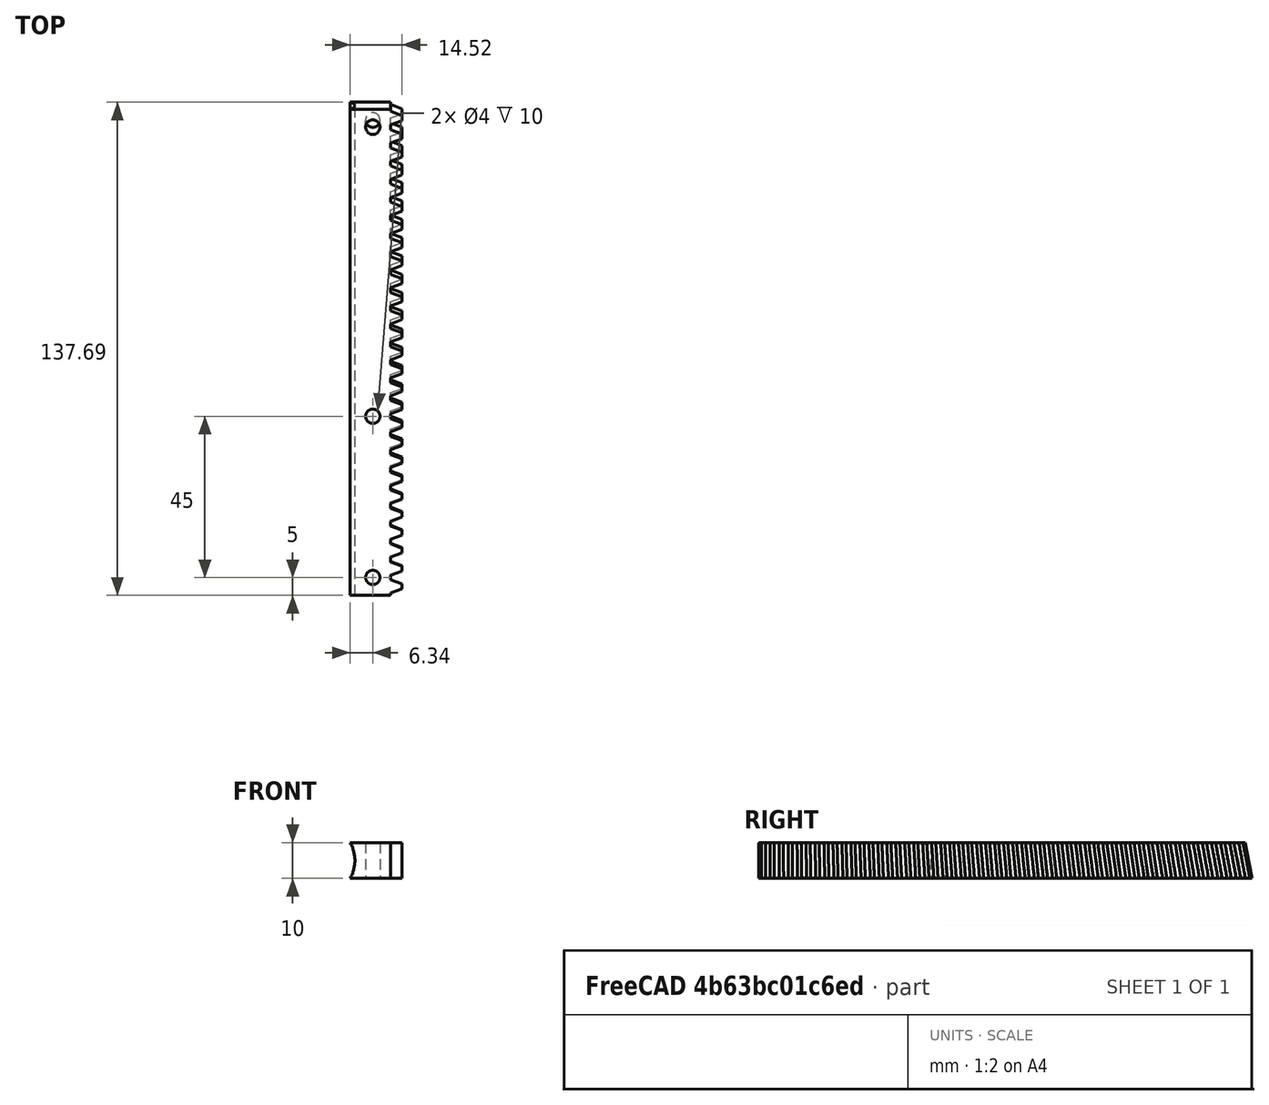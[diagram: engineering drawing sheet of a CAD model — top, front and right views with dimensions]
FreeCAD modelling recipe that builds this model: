
FCSTD DOCUMENT  (FreeCAD 0.17R13522 (Git))
Label: turnrack-rev
License: All rights reserved
LicenseURL: http://en.wikipedia.org/wiki/All_rights_reserved
objects: Part::FeaturePython×27, Part::Cylinder×5, Part::MultiFuse×3, Part::Box×2, Part::Cut×1, Part::Mirroring×1
note: 39 computed .brp shape members not serialized (recipe doc carries the construction recipe); baked Part::Feature solids carry a one-line shape summary decoded from their .brp

FEATURE [Part::FeaturePython] InvoluteRack007  # WARN: FeaturePython — macro-defined, semantics opaque (R4)
  Placement = pos=(0,35.012,0) rot=(0,0,1;0rad)
  beta = 2.91667
  double_helix = false
  head = 0
  height = 10
  module = 1.59155
  pressure_angle = 20
  teeth = 1
  thickness = 10
FEATURE [Part::FeaturePython] InvoluteRack  # WARN: FeaturePython — macro-defined, semantics opaque (R4)
  beta = 0
  double_helix = false
  head = 0
  height = 10
  module = 1.59155
  pressure_angle = 20
  teeth = 1
  thickness = 10
FEATURE [Part::FeaturePython] InvoluteRack004  # WARN: FeaturePython — macro-defined, semantics opaque (R4)
  Placement = pos=(0,20.0019,0) rot=(0,0,1;0rad)
  beta = 1.66667
  double_helix = false
  head = 0
  height = 10
  module = 1.59155
  pressure_angle = 20
  teeth = 1
  thickness = 10
FEATURE [Part::FeaturePython] InvoluteRack003  # WARN: FeaturePython — macro-defined, semantics opaque (R4)
  Placement = pos=(0,15.0007,0) rot=(0,0,1;0rad)
  beta = 1.25
  double_helix = false
  head = 0
  height = 10
  module = 1.59155
  pressure_angle = 20
  teeth = 1
  thickness = 10
FEATURE [Part::FeaturePython] InvoluteRack002  # WARN: FeaturePython — macro-defined, semantics opaque (R4)
  Placement = pos=(0,10.0001,0) rot=(0,0,1;0rad)
  beta = 0.833333
  double_helix = false
  head = 0
  height = 10
  module = 1.59155
  pressure_angle = 20
  teeth = 1
  thickness = 10
FEATURE [Part::FeaturePython] InvoluteRack005  # WARN: FeaturePython — macro-defined, semantics opaque (R4)
  Placement = pos=(0,25.004,0) rot=(0,0,1;0rad)
  beta = 2.08333
  double_helix = false
  head = 0
  height = 10
  module = 1.59155
  pressure_angle = 20
  teeth = 1
  thickness = 10
FEATURE [Part::FeaturePython] InvoluteRack006  # WARN: FeaturePython — macro-defined, semantics opaque (R4)
  Placement = pos=(0,30.0073,0) rot=(0,0,1;0rad)
  beta = 2.5
  double_helix = false
  head = 0
  height = 10
  module = 1.59155
  pressure_angle = 20
  teeth = 1
  thickness = 10
FEATURE [Part::FeaturePython] InvoluteRack001  # WARN: FeaturePython — macro-defined, semantics opaque (R4)
  Placement = pos=(0,5,0) rot=(0,0,1;0rad)
  beta = 0.416667
  double_helix = false
  head = 0
  height = 10
  module = 1.59155
  pressure_angle = 20
  teeth = 1
  thickness = 10
FEATURE [Part::FeaturePython] InvoluteRack008  # WARN: FeaturePython — macro-defined, semantics opaque (R4)
  Placement = pos=(0,40.0185,0) rot=(0,0,1;0rad)
  beta = 3.33333
  double_helix = false
  head = 0
  height = 10
  module = 1.59155
  pressure_angle = 20
  teeth = 1
  thickness = 10
FEATURE [Part::FeaturePython] InvoluteRack009  # WARN: FeaturePython — macro-defined, semantics opaque (R4)
  Placement = pos=(0,45.027,0) rot=(0,0,1;0rad)
  beta = 3.75
  double_helix = false
  head = 0
  height = 10
  module = 1.59155
  pressure_angle = 20
  teeth = 1
  thickness = 10
FEATURE [Part::FeaturePython] InvoluteRack010  # WARN: FeaturePython — macro-defined, semantics opaque (R4)
  Placement = pos=(0,50.0377,0) rot=(0,0,1;0rad)
  beta = 4.16667
  double_helix = false
  head = 0
  height = 10
  module = 1.59155
  pressure_angle = 20
  teeth = 1
  thickness = 10
FEATURE [Part::FeaturePython] InvoluteRack011  # WARN: FeaturePython — macro-defined, semantics opaque (R4)
  Placement = pos=(0,55.051,0) rot=(0,0,1;0rad)
  beta = 4.58333
  double_helix = false
  head = 0
  height = 10
  module = 1.59155
  pressure_angle = 20
  teeth = 1
  thickness = 10
FEATURE [Part::FeaturePython] InvoluteRack012  # WARN: FeaturePython — macro-defined, semantics opaque (R4)
  Placement = pos=(0,60.067,0) rot=(0,0,1;0rad)
  beta = 5
  double_helix = false
  head = 0
  height = 10
  module = 1.59155
  pressure_angle = 20
  teeth = 1
  thickness = 10
FEATURE [Part::FeaturePython] InvoluteRack013  # WARN: FeaturePython — macro-defined, semantics opaque (R4)
  Placement = pos=(0,65.0861,0) rot=(0,0,1;0rad)
  beta = 5.41667
  double_helix = false
  head = 0
  height = 10
  module = 1.59155
  pressure_angle = 20
  teeth = 1
  thickness = 10
FEATURE [Part::FeaturePython] InvoluteRack014  # WARN: FeaturePython — macro-defined, semantics opaque (R4)
  Placement = pos=(0,70.1085,0) rot=(0,0,1;0rad)
  beta = 5.83333
  double_helix = false
  head = 0
  height = 10
  module = 1.59155
  pressure_angle = 20
  teeth = 1
  thickness = 10
FEATURE [Part::FeaturePython] InvoluteRack015  # WARN: FeaturePython — macro-defined, semantics opaque (R4)
  Placement = pos=(0,75.1346,0) rot=(0,0,1;0rad)
  beta = 6.25
  double_helix = false
  head = 0
  height = 10
  module = 1.59155
  pressure_angle = 20
  teeth = 1
  thickness = 10
FEATURE [Part::FeaturePython] InvoluteRack016  # WARN: FeaturePython — macro-defined, semantics opaque (R4)
  Placement = pos=(0,80.1645,0) rot=(0,0,1;0rad)
  beta = 6.66667
  double_helix = false
  head = 0
  height = 10
  module = 1.59155
  pressure_angle = 20
  teeth = 1
  thickness = 10
FEATURE [Part::FeaturePython] InvoluteRack017  # WARN: FeaturePython — macro-defined, semantics opaque (R4)
  Placement = pos=(0,85.1985,0) rot=(0,0,1;0rad)
  beta = 7.08333
  double_helix = false
  head = 0
  height = 10
  module = 1.59155
  pressure_angle = 20
  teeth = 1
  thickness = 10
FEATURE [Part::FeaturePython] InvoluteRack018  # WARN: FeaturePython — macro-defined, semantics opaque (R4)
  Placement = pos=(0,90.237,0) rot=(0,0,1;0rad)
  beta = 7.5
  double_helix = false
  head = 0
  height = 10
  module = 1.59155
  pressure_angle = 20
  teeth = 1
  thickness = 10
FEATURE [Part::FeaturePython] InvoluteRack019  # WARN: FeaturePython — macro-defined, semantics opaque (R4)
  Placement = pos=(0,95.2801,0) rot=(0,0,1;0rad)
  beta = 7.91667
  double_helix = false
  head = 0
  height = 10
  module = 1.59155
  pressure_angle = 20
  teeth = 1
  thickness = 10
FEATURE [Part::FeaturePython] InvoluteRack020  # WARN: FeaturePython — macro-defined, semantics opaque (R4)
  Placement = pos=(0,100.328,0) rot=(0,0,1;0rad)
  beta = 8.33333
  double_helix = false
  head = 0
  height = 10
  module = 1.59155
  pressure_angle = 20
  teeth = 1
  thickness = 10
FEATURE [Part::FeaturePython] InvoluteRack021  # WARN: FeaturePython — macro-defined, semantics opaque (R4)
  Placement = pos=(0,105.382,0) rot=(0,0,1;0rad)
  beta = 8.75
  double_helix = false
  head = 0
  height = 10
  module = 1.59155
  pressure_angle = 20
  teeth = 1
  thickness = 10
FEATURE [Part::FeaturePython] InvoluteRack022  # WARN: FeaturePython — macro-defined, semantics opaque (R4)
  Placement = pos=(0,110.44,0) rot=(0,0,1;0rad)
  beta = 9.16667
  double_helix = false
  head = 0
  height = 10
  module = 1.59155
  pressure_angle = 20
  teeth = 1
  thickness = 10
FEATURE [Part::FeaturePython] InvoluteRack023  # WARN: FeaturePython — macro-defined, semantics opaque (R4)
  Placement = pos=(0,115.505,0) rot=(0,0,1;0rad)
  beta = 9.58333
  double_helix = false
  head = 0
  height = 10
  module = 1.59155
  pressure_angle = 20
  teeth = 1
  thickness = 10
FEATURE [Part::FeaturePython] InvoluteRack024  # WARN: FeaturePython — macro-defined, semantics opaque (R4)
  Placement = pos=(0,120.576,0) rot=(0,0,1;0rad)
  beta = 10
  double_helix = false
  head = 0
  height = 10
  module = 1.59155
  pressure_angle = 20
  teeth = 1
  thickness = 10
FEATURE [Part::FeaturePython] InvoluteRack025  # WARN: FeaturePython — macro-defined, semantics opaque (R4)
  Placement = pos=(0,125.653,0) rot=(0,0,1;0rad)
  beta = 10.4167
  double_helix = false
  head = 0
  height = 10
  module = 1.59155
  pressure_angle = 20
  teeth = 1
  thickness = 10
FEATURE [Part::FeaturePython] InvoluteRack026  # WARN: FeaturePython — macro-defined, semantics opaque (R4)
  Placement = pos=(0,130.737,0) rot=(0,0,1;0rad)
  beta = 10.8333
  double_helix = false
  head = 0
  height = 10
  module = 1.59155
  pressure_angle = 20
  teeth = 1
  thickness = 10
FEATURE [Part::MultiFuse] Union  label="Linear Beta Rack"
  Placement = pos=(11.5915,2.5,0) rot=(0,0,1;0rad)
  Shapes = -> [InvoluteRack,InvoluteRack001,InvoluteRack002,InvoluteRack003,InvoluteRack004,InvoluteRack005,InvoluteRack006,InvoluteRack007,InvoluteRack008,InvoluteRack009,InvoluteRack010,InvoluteRack011,InvoluteRack012,InvoluteRack013,InvoluteRack014,InvoluteRack015,InvoluteRack016,InvoluteRack017,InvoluteRack018,InvoluteRack019,InvoluteRack020,InvoluteRack021,InvoluteRack022,InvoluteRack023,InvoluteRack024,+2 more]
  expr: Placement.Base.x = 10 + 5 / pi
FEATURE [Part::Box] Box  label="Cube"
  AttacherType = Attacher::AttachEngine3D
  Height = 10
  Length = 12
  Placement = pos=(-2,0,0) rot=(0,0,1;0rad)
  Width = 138.25
FEATURE [Part::MultiFuse] Fusion  label="Positive Fusion"
  Shapes = -> [Union,Box]
FEATURE [Part::Box] Box001  label="Cut Off Angle Cube"
  AttacherType = Attacher::AttachEngine3D
  Height = 12
  Length = 12
  Placement = pos=(-2,135.7,0) rot=(-1,0,0;0.19635rad)
  Width = 10
FEATURE [Part::Cylinder] Cylinder  label="Screw Mid"
  Angle = 360
  AttacherType = Attacher::AttachEngine3D
  Height = 10
  Placement = pos=(5,50,0) rot=(0,0,1;0rad)
  Radius = 2
FEATURE [Part::Cylinder] Cylinder002  label="Screw End 2"
  Angle = 360
  AttacherType = Attacher::AttachEngine3D
  Height = 1
  Placement = pos=(5,130.7,0) rot=(1,0,0;2.94524rad)
  Radius = 2
FEATURE [Part::Cylinder] Cylinder001  label="Screw End"
  Angle = 360
  AttacherType = Attacher::AttachEngine3D
  Height = 12
  Placement = pos=(5,130.7,0) rot=(-1,0,0;0.19635rad)
  Radius = 2
FEATURE [Part::Cylinder] Cylinder004  label="Screw Start"
  Angle = 360
  AttacherType = Attacher::AttachEngine3D
  Height = 10
  Placement = pos=(5,5,0) rot=(0,0,1;0rad)
  Radius = 2
FEATURE [Part::Cylinder] Cylinder003  label="Rail Cylinder"
  Angle = 360
  AttacherType = Attacher::AttachEngine3D
  Height = 150
  Placement = pos=(-10,0,5) rot=(-1,0,0;1.5708rad)
  Radius = 10
FEATURE [Part::MultiFuse] Fusion001  label="Negative Fusion"
  Shapes = -> [Box001,Cylinder,Cylinder001,Cylinder002,Cylinder003,Cylinder004]
FEATURE [Part::Cut] Cut
  Base = -> Fusion
  Tool = -> Fusion001
FEATURE [Part::Mirroring] Part__Mirroring  label="Cut (Mirror #1)"
  Base = (0,0,0)
  Normal = (0,0,1)
  Source = -> Cut
